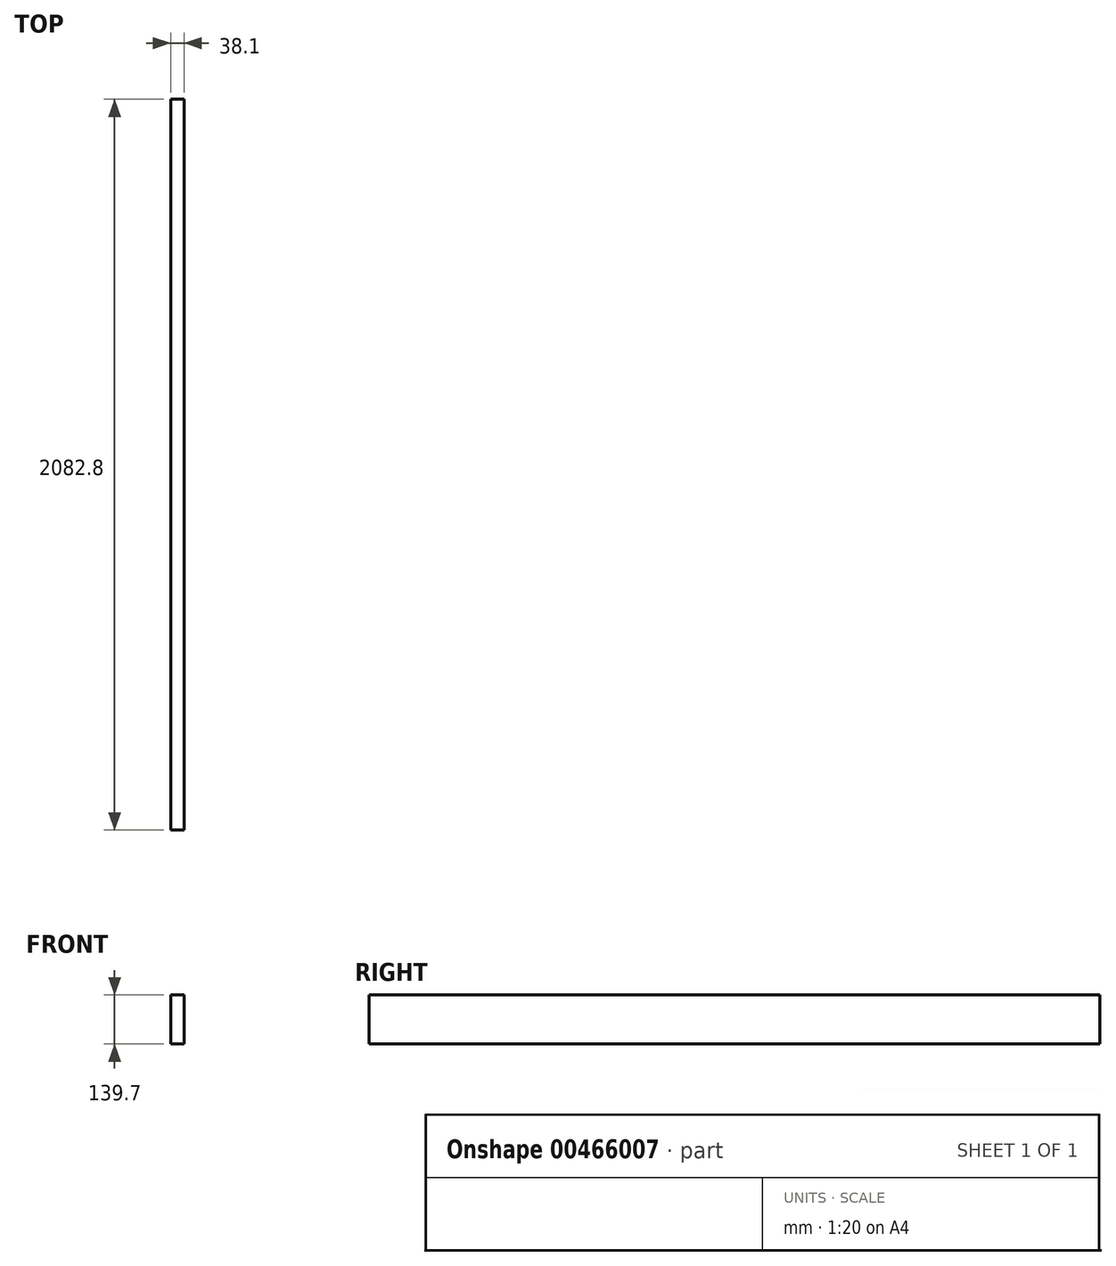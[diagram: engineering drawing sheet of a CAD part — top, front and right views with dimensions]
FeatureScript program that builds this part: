
annotation { "Feature Type Name" : "Feature", "Feature Type Description" : "" }
export const myFeature = defineFeature(function(context is Context, id is Id, definition is map)
    precondition{}
    {
        {
            var Q0;
            Q0=qCreatedBy(makeId("Front.planeOp"),FACE);
            var sketch = newSketch(context, id + "F0", { "sketchPlane" : qUnion([Q0])});
            skLineSegment(sketch, "E0.bottom", {"start": v(19.05, -69.85) * mm, "end": v(-19.05, -69.85) * mm});
            skLineSegment(sketch, "E0.top", {"start": v(19.05, 69.85) * mm, "end": v(-19.05, 69.85) * mm});
            skLineSegment(sketch, "E0.left", {"start": v(19.05, -69.85) * mm, "end": v(19.05, 69.85) * mm});
            skLineSegment(sketch, "E0.right", {"start": v(-19.05, -69.85) * mm, "end": v(-19.05, 69.85) * mm});
            skPoint(sketch, "E0.middle", {"position": v(0, 0) * mm});
            skSolve(sketch);
        }
        {
            var Q0;
            Q0=makeQuery(id+"F0.imprint","IMPRINT",FACE,{"disambiguationData":[TD([[makeQuery(id+"F0.imprint","IMPRINT",EDGE,{"derivedFrom":sQuery(id+"F0.wireOp",EDGE,"E0.bottom")}),-1.0]])]});
            extrude(context, id + "F1", {"entities" : qUnion([Q0]), "endBound" : BoundingType.SYMMETRIC, "depth" : 2082.8 * mm});
        }
        {
            var Q0;
            Q0=makeQuery(id+"F1.opExtrude","SWEPT_BODY",BODY,{"disambiguationData":[OSD([sQuery(id+"F0.wireOp",EDGE,"E0.bottom"),sQuery(id+"F0.wireOp",EDGE,"E0.top"),sQuery(id+"F0.wireOp",EDGE,"E0.left"),sQuery(id+"F0.wireOp",EDGE,"E0.right")])]});
            transform(context, id + "F2", {"entities" : qUnion([Q0]), "transformType" : TransformType.TRANSLATION_3D, "dx" : 127 * mm, "dy" : 0 * mm, "dz" : 0 * mm, "makeCopy" : true});
        }
        {
            var Q0;
            Q0=makeQuery(id+"F2.opPattern","COPY",BODY,{"derivedFrom":makeQuery(id+"F1.opExtrude","SWEPT_BODY",BODY,{"disambiguationData":[OSD([sQuery(id+"F0.wireOp",EDGE,"E0.bottom"),sQuery(id+"F0.wireOp",EDGE,"E0.top"),sQuery(id+"F0.wireOp",EDGE,"E0.left"),sQuery(id+"F0.wireOp",EDGE,"E0.right")])]}),"instanceName":"1"});
            deleteBodies(context, id + "F3", {"entities" : qUnion([Q0])});
        }
    });
